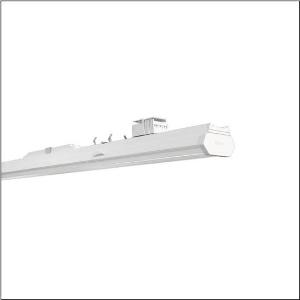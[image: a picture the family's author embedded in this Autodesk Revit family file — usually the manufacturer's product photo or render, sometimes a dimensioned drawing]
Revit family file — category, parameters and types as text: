
# Revit family: licross_11_protected_ho_51td11mn4gxs
name_source: partatom
category: Lighting Fixtures
units: mm (PartAtom-declared; Revit-internal decimal feet)

## family parameters
Cut with Voids When Loaded = No
Host = Face
Light Source = No
Part Type = Normal
Room Calculation Point = No
Round Connector Dimension = Use Diameter
Shared = No

## types (1)
- --- (1 x LED, 16070 lm, 87.4 W, 4000K)
    Apparent Load = 87 VA
    CIE Flux Codes = 84 94 98 99 100
    Color Rendering = 80
    Color Temperature = 4000K
    Default Elevation = 1800 mm
    Description = Licross 11 Protected HO, luminaire insert, of sheet steel, galvanised, coil coated, white, length: 1.500mm, width: 90mm, height: 101mm, LED rated luminous flux: 16.070lm, light colour: 840, SDCM (Standard Deviation of Colour Matching)MacAdam ≤ 2 SDCM (initial), control gear: ON/OFF Multilumen, with plug, 3-pole, with phase selection, mains connection: 220..240V, AC, 50/60Hz, rated input power: 87W, internal wiring halogen-free, primary light control with lens, of plastic, primary optical cover: cover, of PMMA, light emission: direct distribution, primary light characteristic: symmetric, protection rating (complete): IP54, insulation class (complete): insulation class I (protective earthing), certification: CE, ENEC, VDE, UKCA, protection symbol: D if used in an environment with non-conductive dust loads with corresponding accessories, impact resistance: IK06, permissible ambient temperature for indoor applications: -35..+35°C, corresponds to IFS (International Featured Standards) requirements for safety and quality in the food industry, reducing of maximum allowable ambient temperature of 5°C with ceiling mounting, LABS conformity tested according to VDMA 24364:2018-05, The light source and the operating device comply with the requirements of the Ecodesign Regulation (EU) 2019/2020 and are replaceable in accordance with this regulation, packaging unit: 1 piece
    Height = 92 mm
    Lamp = 1 x LED
    Lamp Light Flux = 16070 lm
    Lamp Power = 87.4 W
    Lamp count = 1
    Length = 1500 mm
    Luminous efficacy = 184 lm/W
    Manufacturer = Siteco
    ModVariant = No
    Model = 51TD11MN4GXS
    Mounting Place = Ceiling
    Mounting Type = Pendant
    Number of Poles = 1
    OnlyDefault = Yes
    Power Factor = 1
    Product Name = Licross 11 Protected HO
    Product group = luminaire insert | ceiling pendant
    ProductGroupID = 901
    Protection Class = Protection class I
    Protection Degree = IP 54
    RLX_Detail_Level = 1
    RLX_Emergency_Light_Flux = 0 lm
    RLX_Emergency_Type = 0
    RLX_Emergency_Type_DB = No
    RlxData = <blob elided: 22273 chars, md5=15ce2b16>
    Socket = socket
    Standby Power = 0 W
    System Light Flux = 16070 lm
    System Power = 87 W
    Type Comments = factory setting: luminous flux: 100 % | (A | C | E) | 203 mA
    Type Image = l_1256145.jpg
    URL = http://relux.com
    VarID = @adj_091993
    Voltage = 0 V
    Weight = 0.00 kg
    Width = 88 mm

## geometry (parser evidence)
native form markers: Blend x4, Sweep x9
no freeform markers — native parametric forms only
